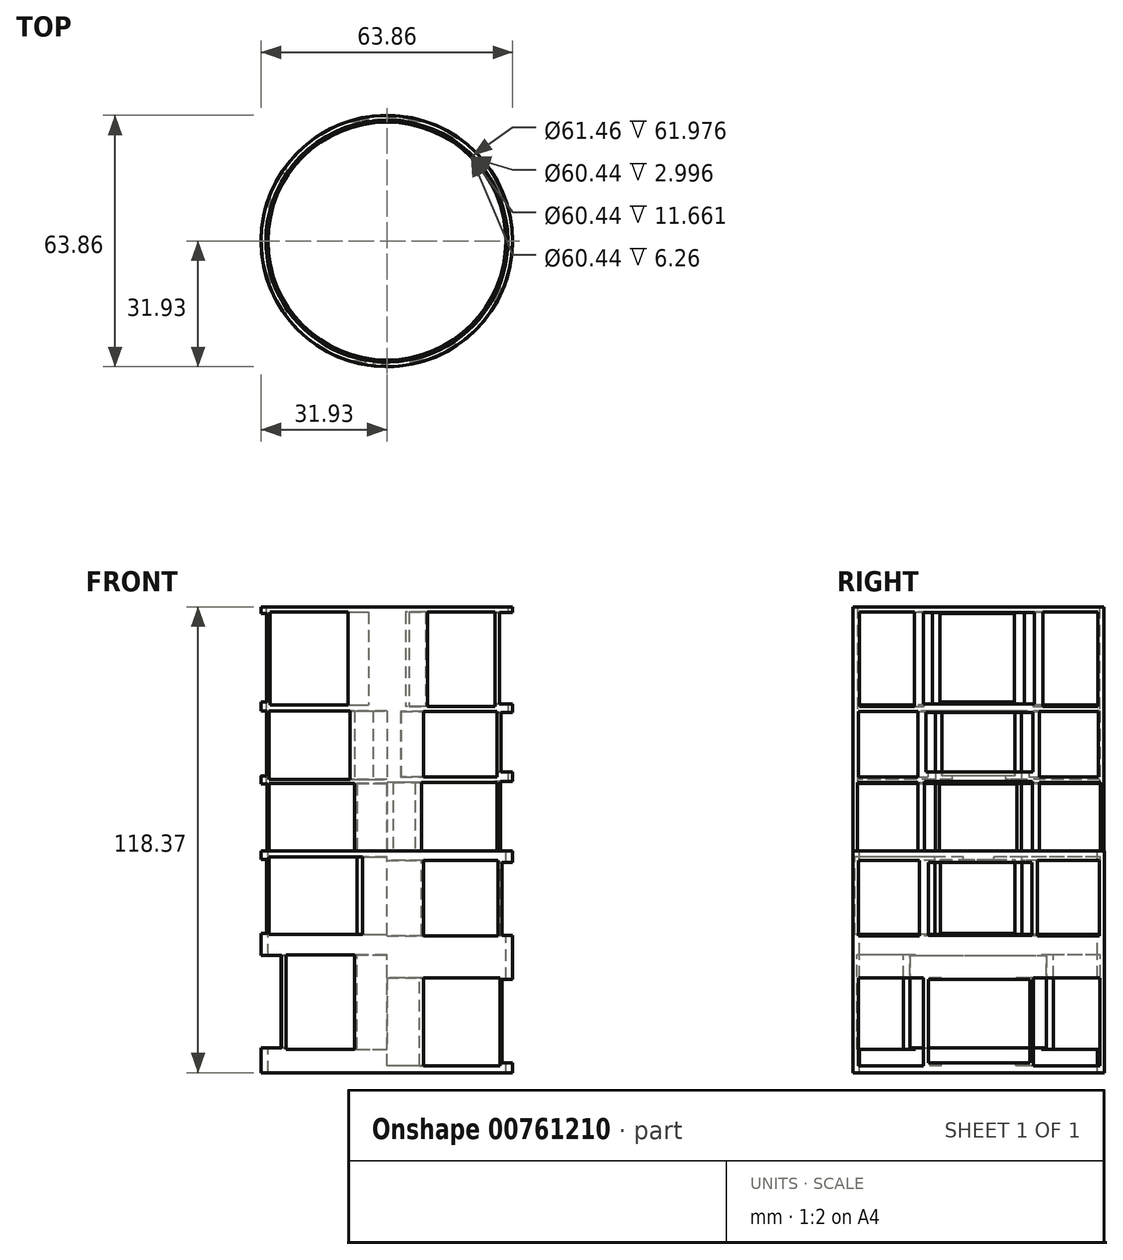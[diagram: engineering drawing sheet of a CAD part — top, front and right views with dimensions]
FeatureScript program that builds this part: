
annotation { "Feature Type Name" : "Feature", "Feature Type Description" : "" }
export const myFeature = defineFeature(function(context is Context, id is Id, definition is map)
    precondition{}
    {
        {
            var Q0;
            Q0=qCreatedBy(makeId("Top.planeOp"),FACE);
            var sketch = newSketch(context, id + "F0", { "sketchPlane" : qUnion([Q0])});
            skCircle(sketch, "E0", {"center": v(0, 0) * mm, "radius": 31.92 * mm});
            skSolve(sketch);
        }
        {
            var Q0;
            Q0 = qSketchRegion(id + "F0", true);
            extrude(context, id + "F1", {"entities" : qUnion([Q0]), "depth" : 61.98 * mm, "offsetDistance" : 25.4 * mm});
        }
        {
            var Q0;
            Q0=qCreatedBy(makeId("Top.planeOp"),FACE);
            var sketch = newSketch(context, id + "F2", { "sketchPlane" : qUnion([Q0])});
            skCircle(sketch, "E1", {"center": v(0, 0) * mm, "radius": 31.93 * mm});
            skSolve(sketch);
        }
        {
            var Q0;
            Q0 = qSketchRegion(id + "F2", true);
            extrude(context, id + "F3", {"entities" : qUnion([Q0]), "operationType" : NewBodyOperationType.ADD, "oppositeDirection" : true, "depth" : 56.4 * mm, "offsetDistance" : 25.4 * mm});
        }
        {
            var Q0;
            Q0=qCreatedBy(makeId("Right.planeOp"),FACE);
            var sketch = newSketch(context, id + "F4", { "sketchPlane" : qUnion([Q0])});
            skLineSegment(sketch, "E2.bottom", {"start": v(31.02, -50.45) * mm, "end": v(-30.85, -50.45) * mm});
            skLineSegment(sketch, "E2.top", {"start": v(31.02, -26.48) * mm, "end": v(-30.85, -26.48) * mm});
            skLineSegment(sketch, "E2.left", {"start": v(31.02, -50.45) * mm, "end": v(31.02, -26.48) * mm});
            skLineSegment(sketch, "E2.right", {"start": v(-30.85, -50.45) * mm, "end": v(-30.85, -26.48) * mm});
            skSolve(sketch);
        }
        {
            var Q0;
            Q0 = qSketchRegion(id + "F4", true);
            extrude(context, id + "F5", {"entities" : qUnion([Q0]), "operationType" : NewBodyOperationType.REMOVE, "oppositeDirection" : true, "depth" : 25.65 * mm, "offsetDistance" : 25.4 * mm});
        }
        {
            var Q0;
            Q0=qCreatedBy(makeId("Right.planeOp"),FACE);
            var sketch = newSketch(context, id + "F6", { "sketchPlane" : qUnion([Q0])});
            skLineSegment(sketch, "E3.bottom", {"start": v(-17.41, -26.64) * mm, "end": v(17.25, -26.64) * mm});
            skLineSegment(sketch, "E3.top", {"start": v(-17.41, -50.13) * mm, "end": v(17.25, -50.13) * mm});
            skLineSegment(sketch, "E3.left", {"start": v(-17.41, -26.64) * mm, "end": v(-17.41, -50.13) * mm});
            skLineSegment(sketch, "E3.right", {"start": v(17.25, -26.64) * mm, "end": v(17.25, -50.13) * mm});
            skSolve(sketch);
        }
        {
            var Q0;
            Q0 = qSketchRegion(id + "F6", true);
            extrude(context, id + "F7", {"entities" : qUnion([Q0]), "operationType" : NewBodyOperationType.REMOVE, "oppositeDirection" : true, "depth" : 55.12 * mm, "offsetDistance" : 25.4 * mm});
        }
        {
            var Q0;
            Q0=qCreatedBy(makeId("Top.planeOp"),FACE);
            var sketch = newSketch(context, id + "F8", { "sketchPlane" : qUnion([Q0])});
            skCircle(sketch, "E4", {"center": v(0, 0) * mm, "radius": 30.22 * mm});
            skSolve(sketch);
        }
        {
            var Q0;
            Q0 = qSketchRegion(id + "F8", true);
            extrude(context, id + "F9", {"entities" : qUnion([Q0]), "operationType" : NewBodyOperationType.REMOVE, "oppositeDirection" : true, "depth" : 86.61 * mm, "offsetDistance" : 25.4 * mm});
        }
        {
            var Q0;
            Q0=qCreatedBy(makeId("Right.planeOp"),FACE);
            var sketch = newSketch(context, id + "F10", { "sketchPlane" : qUnion([Q0])});
            skLineSegment(sketch, "E5.bottom", {"start": v(30.85, -32.31) * mm, "end": v(-30.53, -32.31) * mm});
            skLineSegment(sketch, "E5.top", {"start": v(30.85, -54.66) * mm, "end": v(-30.53, -54.66) * mm});
            skLineSegment(sketch, "E5.left", {"start": v(30.85, -32.31) * mm, "end": v(30.85, -54.66) * mm});
            skLineSegment(sketch, "E5.right", {"start": v(-30.53, -32.31) * mm, "end": v(-30.53, -54.66) * mm});
            skSolve(sketch);
        }
        {
            var Q0;
            Q0 = qSketchRegion(id + "F10", true);
            extrude(context, id + "F11", {"entities" : qUnion([Q0]), "operationType" : NewBodyOperationType.REMOVE, "depth" : 28.7 * mm, "offsetDistance" : 25.4 * mm});
        }
        {
            var Q0;
            Q0=qCreatedBy(makeId("Right.planeOp"),FACE);
            var sketch = newSketch(context, id + "F12", { "sketchPlane" : qUnion([Q0])});
            skLineSegment(sketch, "E6.bottom", {"start": v(13.04, -32.64) * mm, "end": v(-12.71, -32.64) * mm});
            skLineSegment(sketch, "E6.top", {"start": v(13.04, -53.85) * mm, "end": v(-12.71, -53.85) * mm});
            skLineSegment(sketch, "E6.left", {"start": v(13.04, -32.64) * mm, "end": v(13.04, -53.85) * mm});
            skLineSegment(sketch, "E6.right", {"start": v(-12.71, -32.64) * mm, "end": v(-12.71, -53.85) * mm});
            skSolve(sketch);
        }
        {
            var Q0;
            Q0 = qSketchRegion(id + "F12", true);
            extrude(context, id + "F13", {"entities" : qUnion([Q0]), "operationType" : NewBodyOperationType.REMOVE, "depth" : 55.63 * mm, "offsetDistance" : 25.4 * mm});
        }
        {
            var Q0;
            Q0=qCreatedBy(makeId("Right.planeOp"),FACE);
            var sketch = newSketch(context, id + "F14", { "sketchPlane" : qUnion([Q0])});
            skLineSegment(sketch, "E7.bottom", {"start": v(30.7, -21.62) * mm, "end": v(-30.53, -21.62) * mm});
            skLineSegment(sketch, "E7.top", {"start": v(30.7, -2.51) * mm, "end": v(-30.53, -2.51) * mm});
            skLineSegment(sketch, "E7.left", {"start": v(30.7, -21.62) * mm, "end": v(30.7, -2.51) * mm});
            skLineSegment(sketch, "E7.right", {"start": v(-30.53, -21.62) * mm, "end": v(-30.53, -2.51) * mm});
            skSolve(sketch);
        }
        {
            var Q0;
            Q0 = qSketchRegion(id + "F14", true);
            extrude(context, id + "F15", {"entities" : qUnion([Q0]), "operationType" : NewBodyOperationType.REMOVE, "depth" : 28.2 * mm, "offsetDistance" : 25.4 * mm});
        }
        {
            var Q0;
            Q0=qCreatedBy(makeId("Right.planeOp"),FACE);
            var sketch = newSketch(context, id + "F16", { "sketchPlane" : qUnion([Q0])});
            skLineSegment(sketch, "E8.bottom", {"start": v(31.02, -21.3) * mm, "end": v(-31.34, -21.3) * mm});
            skLineSegment(sketch, "E8.top", {"start": v(31.02, -1.54) * mm, "end": v(-31.34, -1.54) * mm});
            skLineSegment(sketch, "E8.left", {"start": v(31.02, -21.3) * mm, "end": v(31.02, -1.54) * mm});
            skLineSegment(sketch, "E8.right", {"start": v(-31.34, -21.3) * mm, "end": v(-31.34, -1.54) * mm});
            skSolve(sketch);
        }
        {
            var Q0;
            Q0 = qSketchRegion(id + "F16", true);
            extrude(context, id + "F17", {"entities" : qUnion([Q0]), "operationType" : NewBodyOperationType.REMOVE, "oppositeDirection" : true, "depth" : 29.97 * mm, "offsetDistance" : 25.4 * mm});
        }
        {
            var Q0;
            Q0=qCreatedBy(makeId("Right.planeOp"),FACE);
            var sketch = newSketch(context, id + "F18", { "sketchPlane" : qUnion([Q0])});
            skLineSegment(sketch, "E9.bottom", {"start": v(-9.64, -2.19) * mm, "end": v(9.31, -2.19) * mm});
            skLineSegment(sketch, "E9.top", {"start": v(-9.64, -20.97) * mm, "end": v(9.31, -20.97) * mm});
            skLineSegment(sketch, "E9.left", {"start": v(-9.64, -2.19) * mm, "end": v(-9.64, -20.97) * mm});
            skLineSegment(sketch, "E9.right", {"start": v(9.31, -2.19) * mm, "end": v(9.31, -20.97) * mm});
            skSolve(sketch);
        }
        {
            var Q0;
            Q0 = qSketchRegion(id + "F18", true);
            extrude(context, id + "F19", {"entities" : qUnion([Q0]), "operationType" : NewBodyOperationType.REMOVE, "oppositeDirection" : true, "depth" : 42.16 * mm, "offsetDistance" : 25.4 * mm});
        }
        {
            var Q0;
            Q0=qCreatedBy(makeId("Right.planeOp"),FACE);
            var sketch = newSketch(context, id + "F20", { "sketchPlane" : qUnion([Q0])});
            skLineSegment(sketch, "E10.bottom", {"start": v(13.52, -3) * mm, "end": v(-12.71, -3) * mm});
            skLineSegment(sketch, "E10.top", {"start": v(13.52, -21.46) * mm, "end": v(-12.71, -21.46) * mm});
            skLineSegment(sketch, "E10.left", {"start": v(13.52, -3) * mm, "end": v(13.52, -21.46) * mm});
            skLineSegment(sketch, "E10.right", {"start": v(-12.71, -3) * mm, "end": v(-12.71, -21.46) * mm});
            skSolve(sketch);
        }
        {
            var Q0;
            Q0 = qSketchRegion(id + "F20", true);
            extrude(context, id + "F21", {"entities" : qUnion([Q0]), "operationType" : NewBodyOperationType.REMOVE, "depth" : 48 * mm, "offsetDistance" : 25.4 * mm});
        }
        {
            var Q0;
            Q0=qCreatedBy(makeId("Right.planeOp"),FACE);
            var sketch = newSketch(context, id + "F22", { "sketchPlane" : qUnion([Q0])});
            skLineSegment(sketch, "E11.bottom", {"start": v(-30.85, 17.09) * mm, "end": v(31.02, 17.09) * mm});
            skLineSegment(sketch, "E11.top", {"start": v(-30.85, 0) * mm, "end": v(31.02, 0) * mm});
            skLineSegment(sketch, "E11.left", {"start": v(-30.85, 17.09) * mm, "end": v(-30.85, 0) * mm});
            skLineSegment(sketch, "E11.right", {"start": v(31.02, 17.09) * mm, "end": v(31.02, 0) * mm});
            skSolve(sketch);
        }
        {
            var Q0;
            Q0 = qSketchRegion(id + "F22", true);
            extrude(context, id + "F23", {"entities" : qUnion([Q0]), "operationType" : NewBodyOperationType.REMOVE, "oppositeDirection" : true, "depth" : 29.97 * mm, "offsetDistance" : 25.4 * mm});
        }
        {
            var Q0;
            Q0=qCreatedBy(makeId("Right.planeOp"),FACE);
            var sketch = newSketch(context, id + "F24", { "sketchPlane" : qUnion([Q0])});
            skLineSegment(sketch, "E12.bottom", {"start": v(-30.7, 0) * mm, "end": v(31.11, 0) * mm});
            skLineSegment(sketch, "E12.top", {"start": v(-30.7, 17.33) * mm, "end": v(31.11, 17.33) * mm});
            skLineSegment(sketch, "E12.left", {"start": v(-30.7, 0) * mm, "end": v(-30.7, 17.33) * mm});
            skLineSegment(sketch, "E12.right", {"start": v(31.11, 0) * mm, "end": v(31.11, 17.33) * mm});
            skSolve(sketch);
        }
        {
            var Q0;
            Q0 = qSketchRegion(id + "F24", true);
            extrude(context, id + "F25", {"entities" : qUnion([Q0]), "operationType" : NewBodyOperationType.REMOVE, "depth" : 27.94 * mm, "offsetDistance" : 25.4 * mm});
        }
        {
            var Q0;
            Q0=qCreatedBy(makeId("Right.planeOp"),FACE);
            var sketch = newSketch(context, id + "F26", { "sketchPlane" : qUnion([Q0])});
            skLineSegment(sketch, "E13.bottom", {"start": v(9.8, 0) * mm, "end": v(-9.96, 0) * mm});
            skLineSegment(sketch, "E13.top", {"start": v(9.8, 16.93) * mm, "end": v(-9.96, 16.93) * mm});
            skLineSegment(sketch, "E13.left", {"start": v(9.8, 0) * mm, "end": v(9.8, 16.93) * mm});
            skLineSegment(sketch, "E13.right", {"start": v(-9.96, 0) * mm, "end": v(-9.96, 16.93) * mm});
            skSolve(sketch);
        }
        {
            var Q0;
            Q0 = qSketchRegion(id + "F26", true);
            extrude(context, id + "F27", {"entities" : qUnion([Q0]), "operationType" : NewBodyOperationType.REMOVE, "oppositeDirection" : true, "depth" : 59.94 * mm, "offsetDistance" : 25.4 * mm});
        }
        {
            var Q0;
            Q0=qCreatedBy(makeId("Right.planeOp"),FACE);
            var sketch = newSketch(context, id + "F28", { "sketchPlane" : qUnion([Q0])});
            skLineSegment(sketch, "E14.bottom", {"start": v(-13.69, 0) * mm, "end": v(13.69, 0) * mm});
            skLineSegment(sketch, "E14.top", {"start": v(-13.69, 17.57) * mm, "end": v(13.69, 17.57) * mm});
            skLineSegment(sketch, "E14.left", {"start": v(-13.69, 0) * mm, "end": v(-13.69, 17.57) * mm});
            skLineSegment(sketch, "E14.right", {"start": v(13.69, 0) * mm, "end": v(13.69, 17.57) * mm});
            skSolve(sketch);
        }
        {
            var Q0;
            Q0 = qSketchRegion(id + "F28", true);
            extrude(context, id + "F29", {"entities" : qUnion([Q0]), "operationType" : NewBodyOperationType.REMOVE, "depth" : 67.56 * mm, "offsetDistance" : 25.4 * mm});
        }
        {
            var Q0;
            Q0=qCreatedBy(makeId("Top.planeOp"),FACE);
            var sketch = newSketch(context, id + "F30", { "sketchPlane" : qUnion([Q0])});
            skCircle(sketch, "E15", {"center": v(0, 0) * mm, "radius": 30.73 * mm});
            skSolve(sketch);
        }
        {
            var Q0;
            Q0 = qSketchRegion(id + "F30", true);
            extrude(context, id + "F31", {"entities" : qUnion([Q0]), "operationType" : NewBodyOperationType.REMOVE, "depth" : 121.4 * mm, "offsetDistance" : 25.4 * mm});
        }
        {
            var Q0;
            Q0=qCreatedBy(makeId("Right.planeOp"),FACE);
            var sketch = newSketch(context, id + "F32", { "sketchPlane" : qUnion([Q0])});
            skLineSegment(sketch, "E16.bottom", {"start": v(30.85, 18.06) * mm, "end": v(-30.53, 18.06) * mm});
            skLineSegment(sketch, "E16.top", {"start": v(30.85, 35.55) * mm, "end": v(-30.53, 35.55) * mm});
            skLineSegment(sketch, "E16.left", {"start": v(30.85, 18.06) * mm, "end": v(30.85, 35.55) * mm});
            skLineSegment(sketch, "E16.right", {"start": v(-30.53, 18.06) * mm, "end": v(-30.53, 35.55) * mm});
            skSolve(sketch);
        }
        {
            var Q0;
            Q0 = qSketchRegion(id + "F32", true);
            extrude(context, id + "F33", {"entities" : qUnion([Q0]), "operationType" : NewBodyOperationType.REMOVE, "oppositeDirection" : true, "depth" : 29.97 * mm, "offsetDistance" : 25.4 * mm});
        }
        {
            var Q0;
            Q0=qCreatedBy(makeId("Right.planeOp"),FACE);
            var sketch = newSketch(context, id + "F34", { "sketchPlane" : qUnion([Q0])});
            skLineSegment(sketch, "E17.bottom", {"start": v(-30.53, 18.7) * mm, "end": v(30.51, 18.7) * mm});
            skLineSegment(sketch, "E17.top", {"start": v(-30.53, 35.33) * mm, "end": v(30.51, 35.33) * mm});
            skLineSegment(sketch, "E17.left", {"start": v(-30.53, 18.7) * mm, "end": v(-30.53, 35.33) * mm});
            skLineSegment(sketch, "E17.right", {"start": v(30.51, 18.7) * mm, "end": v(30.51, 35.33) * mm});
            skSolve(sketch);
        }
        {
            var Q0;
            Q0 = qSketchRegion(id + "F34", true);
            extrude(context, id + "F35", {"entities" : qUnion([Q0]), "operationType" : NewBodyOperationType.REMOVE, "depth" : 27.94 * mm, "offsetDistance" : 25.4 * mm});
        }
        {
            var Q0;
            Q0=qCreatedBy(makeId("Right.planeOp"),FACE);
            var sketch = newSketch(context, id + "F36", { "sketchPlane" : qUnion([Q0])});
            skLineSegment(sketch, "E18.bottom", {"start": v(-13.36, 20) * mm, "end": v(13.85, 20) * mm});
            skLineSegment(sketch, "E18.top", {"start": v(-13.36, 35.07) * mm, "end": v(13.85, 35.07) * mm});
            skLineSegment(sketch, "E18.left", {"start": v(-13.36, 20) * mm, "end": v(-13.36, 35.07) * mm});
            skLineSegment(sketch, "E18.right", {"start": v(13.85, 20) * mm, "end": v(13.85, 35.07) * mm});
            skSolve(sketch);
        }
        {
            var Q0;
            Q0 = qSketchRegion(id + "F36", true);
            extrude(context, id + "F37", {"entities" : qUnion([Q0]), "operationType" : NewBodyOperationType.REMOVE, "depth" : 51.05 * mm, "offsetDistance" : 25.4 * mm});
        }
        {
            var Q0;
            Q0=qCreatedBy(makeId("Right.planeOp"),FACE);
            var sketch = newSketch(context, id + "F38", { "sketchPlane" : qUnion([Q0])});
            skLineSegment(sketch, "E19.bottom", {"start": v(9.31, 19.03) * mm, "end": v(-9.31, 19.03) * mm});
            skLineSegment(sketch, "E19.top", {"start": v(9.31, 35.55) * mm, "end": v(-9.31, 35.55) * mm});
            skLineSegment(sketch, "E19.left", {"start": v(9.31, 19.03) * mm, "end": v(9.31, 35.55) * mm});
            skLineSegment(sketch, "E19.right", {"start": v(-9.31, 19.03) * mm, "end": v(-9.31, 35.55) * mm});
            skSolve(sketch);
        }
        {
            var Q0;
            Q0 = qSketchRegion(id + "F38", true);
            extrude(context, id + "F39", {"entities" : qUnion([Q0]), "operationType" : NewBodyOperationType.REMOVE, "oppositeDirection" : true, "depth" : 66.3 * mm, "offsetDistance" : 25.4 * mm});
        }
        {
            var Q0;
            Q0=qCreatedBy(makeId("Right.planeOp"),FACE);
            var sketch = newSketch(context, id + "F40", { "sketchPlane" : qUnion([Q0])});
            skLineSegment(sketch, "E20.bottom", {"start": v(-30.2, 36.68) * mm, "end": v(30.37, 36.68) * mm});
            skLineSegment(sketch, "E20.top", {"start": v(-30.2, 60.66) * mm, "end": v(30.37, 60.66) * mm});
            skLineSegment(sketch, "E20.left", {"start": v(-30.2, 36.68) * mm, "end": v(-30.2, 60.66) * mm});
            skLineSegment(sketch, "E20.right", {"start": v(30.37, 36.68) * mm, "end": v(30.37, 60.66) * mm});
            skSolve(sketch);
        }
        {
            var Q0;
            Q0 = qSketchRegion(id + "F40", true);
            extrude(context, id + "F41", {"entities" : qUnion([Q0]), "operationType" : NewBodyOperationType.REMOVE, "depth" : 27.43 * mm, "offsetDistance" : 25.4 * mm});
        }
        {
            var Q0;
            Q0=qCreatedBy(makeId("Right.planeOp"),FACE);
            var sketch = newSketch(context, id + "F42", { "sketchPlane" : qUnion([Q0])});
            skLineSegment(sketch, "E21.bottom", {"start": v(-14, 37.33) * mm, "end": v(14.17, 37.33) * mm});
            skLineSegment(sketch, "E21.top", {"start": v(-14, 60.5) * mm, "end": v(14.17, 60.5) * mm});
            skLineSegment(sketch, "E21.left", {"start": v(-14, 37.33) * mm, "end": v(-14, 60.5) * mm});
            skLineSegment(sketch, "E21.right", {"start": v(14.17, 37.33) * mm, "end": v(14.17, 60.5) * mm});
            skSolve(sketch);
        }
        {
            var Q0;
            Q0 = qSketchRegion(id + "F42", true);
            extrude(context, id + "F43", {"entities" : qUnion([Q0]), "operationType" : NewBodyOperationType.REMOVE, "depth" : 40.9 * mm, "offsetDistance" : 25.4 * mm});
        }
        {
            var Q0;
            Q0=qCreatedBy(makeId("Right.planeOp"),FACE);
            var sketch = newSketch(context, id + "F44", { "sketchPlane" : qUnion([Q0])});
            skLineSegment(sketch, "E22.bottom", {"start": v(30.37, 37) * mm, "end": v(-30.37, 37) * mm});
            skLineSegment(sketch, "E22.top", {"start": v(30.37, 60.66) * mm, "end": v(-30.37, 60.66) * mm});
            skLineSegment(sketch, "E22.left", {"start": v(30.37, 37) * mm, "end": v(30.37, 60.66) * mm});
            skLineSegment(sketch, "E22.right", {"start": v(-30.37, 37) * mm, "end": v(-30.37, 60.66) * mm});
            skSolve(sketch);
        }
        {
            var Q0;
            Q0 = qSketchRegion(id + "F44", true);
            extrude(context, id + "F45", {"entities" : qUnion([Q0]), "operationType" : NewBodyOperationType.REMOVE, "oppositeDirection" : true, "depth" : 29.72 * mm, "offsetDistance" : 25.4 * mm});
        }
        {
            var Q0;
            Q0=qCreatedBy(makeId("Right.planeOp"),FACE);
            var sketch = newSketch(context, id + "F46", { "sketchPlane" : qUnion([Q0])});
            skLineSegment(sketch, "E23.bottom", {"start": v(9.15, 37.82) * mm, "end": v(-9.8, 37.82) * mm});
            skLineSegment(sketch, "E23.top", {"start": v(9.15, 60.33) * mm, "end": v(-9.8, 60.33) * mm});
            skLineSegment(sketch, "E23.left", {"start": v(9.15, 37.82) * mm, "end": v(9.15, 60.33) * mm});
            skLineSegment(sketch, "E23.right", {"start": v(-9.8, 37.82) * mm, "end": v(-9.8, 60.33) * mm});
            skSolve(sketch);
        }
        {
            var Q0;
            Q0 = qSketchRegion(id + "F46", true);
            extrude(context, id + "F47", {"entities" : qUnion([Q0]), "operationType" : NewBodyOperationType.REMOVE, "oppositeDirection" : true, "depth" : 43.18 * mm, "offsetDistance" : 25.4 * mm});
        }
    });
